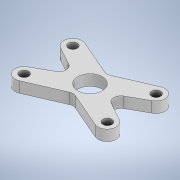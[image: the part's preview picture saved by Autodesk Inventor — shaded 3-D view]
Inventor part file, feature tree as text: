
AUTODESK INVENTOR PART (.ipt)
format: ipt  version: 2021 (Build 250183000, 183)  size: 134,144 bytes
history: native  units: mm
features: other x1, extrude x1, sketch x1
ambient origin geometry x8: Origin, YZ Plane, XZ Plane, XY Plane, X Axis, Y Axis, Z Axis, Center Point
bodies: Body1 (feature_tree)
feature tree (3):
  other  "Sólido1"
  extrude  "Extrusión1"  [1 undecoded]
  sketch  "Boceto1"  dims[d14=3.0mm d15=0.0mm]
note: 1 required parameter value undecoded (feature->parameter linkage not recoverable at this tier; creation-order binding heuristic only, values carry confidence <= 0.55)
